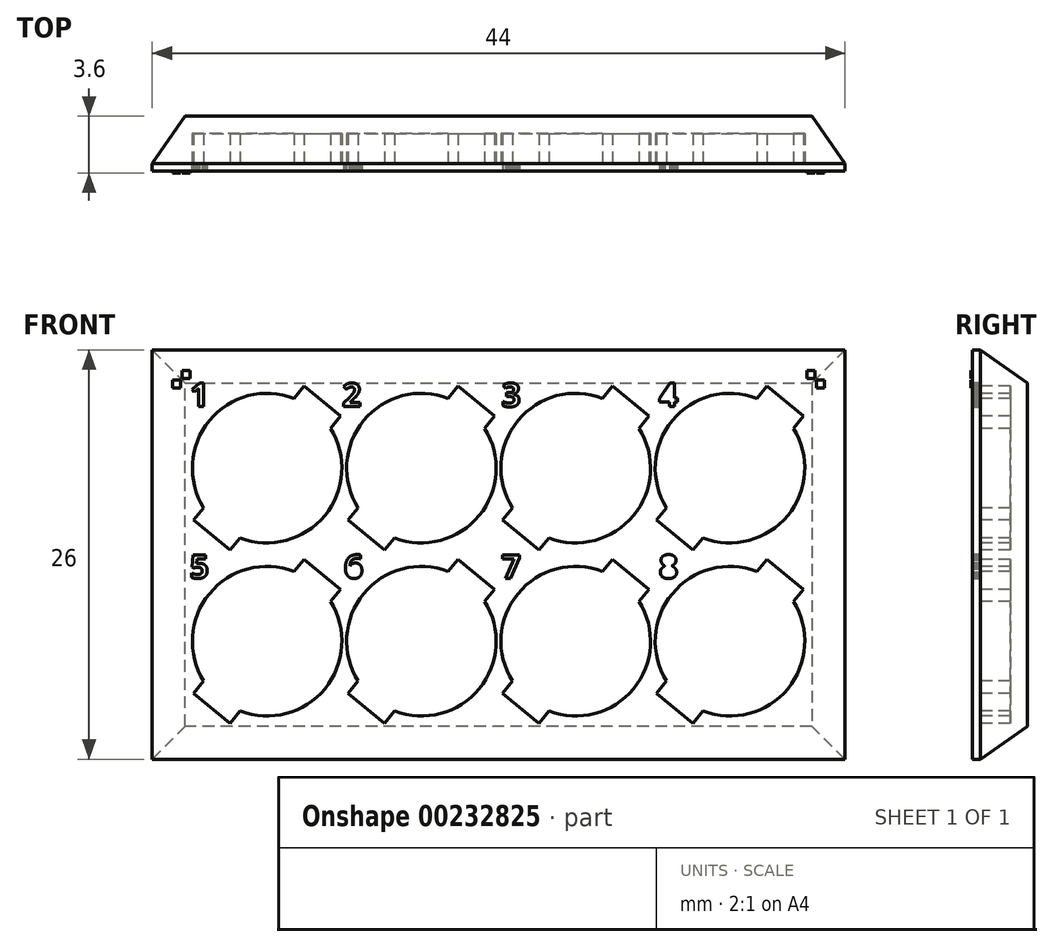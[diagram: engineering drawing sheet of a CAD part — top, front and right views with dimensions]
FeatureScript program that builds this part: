
annotation { "Feature Type Name" : "Feature", "Feature Type Description" : "" }
export const myFeature = defineFeature(function(context is Context, id is Id, definition is map)
    precondition{}
    {
        {
            var Q0;
            Q0=qCreatedBy(makeId("Front.planeOp"),FACE);
            var sketch = newSketch(context, id + "F0", { "sketchPlane" : qUnion([Q0])});
            skLineSegment(sketch, "E0.bottom", {"start": v(4.9, -5.5) * mm, "end": v(-4.9, -5.5) * mm});
            skLineSegment(sketch, "E0.top", {"start": v(4.9, 5.5) * mm, "end": v(-4.9, 5.5) * mm});
            skLineSegment(sketch, "E0.left", {"start": v(4.9, -5.5) * mm, "end": v(4.9, 5.5) * mm});
            skLineSegment(sketch, "E0.right", {"start": v(-4.9, -5.5) * mm, "end": v(-4.9, 5.5) * mm});
            skPoint(sketch, "E0.middle", {"position": v(0, 0) * mm});
            skSolve(sketch);
        }
        {
            var Q0;
            Q0=qSketchRegion(id+"F0",true);
            extrude(context, id + "F1", {"entities" : qUnion([Q0]), "oppositeDirection" : true, "depth" : 3.5 * mm, "offsetDistance" : 25 * mm});
        }
        {
            var Q0;
            Q0=qCreatedBy(makeId("Front.planeOp"),FACE);
            var sketch = newSketch(context, id + "F2", { "sketchPlane" : qUnion([Q0])});
            skCircle(sketch, "E1", {"center": v(0, 0) * mm, "radius": 4.75 * mm});
            skLineSegment(sketch, "E2", {"start": v(1.7, 4.43) * mm, "end": v(2.34, 5.2) * mm});
            skLineSegment(sketch, "E3", {"start": v(2.34, 5.2) * mm, "end": v(4.66, 3.3) * mm});
            skLineSegment(sketch, "E4", {"start": v(4.66, 3.3) * mm, "end": v(4.02, 2.53) * mm});
            skLineSegment(sketch, "E5", {"start": v(-4.02, -2.53) * mm, "end": v(-4.66, -3.3) * mm});
            skLineSegment(sketch, "E6", {"start": v(-4.66, -3.3) * mm, "end": v(-2.34, -5.2) * mm});
            skLineSegment(sketch, "E7", {"start": v(-2.34, -5.2) * mm, "end": v(-1.7, -4.43) * mm});
            skSolve(sketch);
        }
        {
            var Q0;
            Q0=qSketchRegion(id+"F2",true);
            extrude(context, id + "F3", {"entities" : qUnion([Q0]), "operationType" : NewBodyOperationType.REMOVE, "oppositeDirection" : true, "depth" : 2.4 * mm, "offsetDistance" : 25 * mm});
        }
        {
            var Q0;
            Q0=makeQuery(id+"F1.opExtrude","SWEPT_BODY",BODY,{"disambiguationData":[OSD([sQuery(id+"F0.wireOp",EDGE,"E0.bottom"),sQuery(id+"F0.wireOp",EDGE,"E0.top"),sQuery(id+"F0.wireOp",EDGE,"E0.left"),sQuery(id+"F0.wireOp",EDGE,"E0.right")])]});
            transform(context, id + "F4", {"entities" : qUnion([Q0]), "transformType" : TransformType.TRANSLATION_3D, "dx" : -9.8 * mm, "dy" : 0 * mm, "dz" : 0 * mm, "makeCopy" : true});
        }
        {
            var Q0;
            Q0=makeQuery(id+"F1.opExtrude","SWEPT_BODY",BODY,{"disambiguationData":[OSD([sQuery(id+"F0.wireOp",EDGE,"E0.bottom"),sQuery(id+"F0.wireOp",EDGE,"E0.top"),sQuery(id+"F0.wireOp",EDGE,"E0.left"),sQuery(id+"F0.wireOp",EDGE,"E0.right")])]});
            transform(context, id + "F5", {"entities" : qUnion([Q0]), "transformType" : TransformType.TRANSLATION_3D, "dx" : 0 * mm, "dy" : 0 * mm, "dz" : 11 * mm, "makeCopy" : true});
        }
        {
            var Q0;
            Q0=makeQuery(id+"F1.opExtrude","SWEPT_BODY",BODY,{"disambiguationData":[OSD([sQuery(id+"F0.wireOp",EDGE,"E0.bottom"),sQuery(id+"F0.wireOp",EDGE,"E0.top"),sQuery(id+"F0.wireOp",EDGE,"E0.left"),sQuery(id+"F0.wireOp",EDGE,"E0.right")])]});
            transform(context, id + "F6", {"entities" : qUnion([Q0]), "transformType" : TransformType.TRANSLATION_3D, "dx" : -9.8 * mm, "dy" : 0 * mm, "dz" : 11 * mm, "makeCopy" : true});
        }
        {
            var Q0;
            Q0=makeQuery(id+"F1.opExtrude","SWEPT_BODY",BODY,{"disambiguationData":[OSD([sQuery(id+"F0.wireOp",EDGE,"E0.bottom"),sQuery(id+"F0.wireOp",EDGE,"E0.top"),sQuery(id+"F0.wireOp",EDGE,"E0.left"),sQuery(id+"F0.wireOp",EDGE,"E0.right")])]});
            var Q1;
            Q1=makeQuery(id+"F4.opPattern","COPY",BODY,{"derivedFrom":makeQuery(id+"F1.opExtrude","SWEPT_BODY",BODY,{"disambiguationData":[OSD([sQuery(id+"F0.wireOp",EDGE,"E0.bottom"),sQuery(id+"F0.wireOp",EDGE,"E0.top"),sQuery(id+"F0.wireOp",EDGE,"E0.left"),sQuery(id+"F0.wireOp",EDGE,"E0.right")])]}),"instanceName":"1"});
            var Q2;
            Q2=makeQuery(id+"F5.opPattern","COPY",BODY,{"derivedFrom":makeQuery(id+"F1.opExtrude","SWEPT_BODY",BODY,{"disambiguationData":[OSD([sQuery(id+"F0.wireOp",EDGE,"E0.bottom"),sQuery(id+"F0.wireOp",EDGE,"E0.top"),sQuery(id+"F0.wireOp",EDGE,"E0.left"),sQuery(id+"F0.wireOp",EDGE,"E0.right")])]}),"instanceName":"1"});
            var Q3;
            Q3=makeQuery(id+"F6.opPattern","COPY",BODY,{"derivedFrom":makeQuery(id+"F1.opExtrude","SWEPT_BODY",BODY,{"disambiguationData":[OSD([sQuery(id+"F0.wireOp",EDGE,"E0.bottom"),sQuery(id+"F0.wireOp",EDGE,"E0.top"),sQuery(id+"F0.wireOp",EDGE,"E0.left"),sQuery(id+"F0.wireOp",EDGE,"E0.right")])]}),"instanceName":"1"});
            booleanBodies(context, id + "F7", {"operationType" : BooleanOperationType.UNION, "tools" : qUnion([Q0, Q1, Q2, Q3])});
        }
        {
            var Q0;
            Q0=makeQuery(id+"F1.opExtrude","SWEPT_BODY",BODY,{"disambiguationData":[OSD([sQuery(id+"F0.wireOp",EDGE,"E0.bottom"),sQuery(id+"F0.wireOp",EDGE,"E0.top"),sQuery(id+"F0.wireOp",EDGE,"E0.left"),sQuery(id+"F0.wireOp",EDGE,"E0.right")])]});
            transform(context, id + "F8", {"entities" : qUnion([Q0]), "transformType" : TransformType.TRANSLATION_3D, "dx" : 19.6 * mm, "dy" : 0 * mm, "dz" : 0 * mm, "makeCopy" : true});
        }
        {
            var Q0;
            Q0=makeQuery(id+"F1.opExtrude","SWEPT_BODY",BODY,{"disambiguationData":[OSD([sQuery(id+"F0.wireOp",EDGE,"E0.bottom"),sQuery(id+"F0.wireOp",EDGE,"E0.top"),sQuery(id+"F0.wireOp",EDGE,"E0.left"),sQuery(id+"F0.wireOp",EDGE,"E0.right")])]});
            var Q1;
            Q1=makeQuery(id+"F8.opPattern","COPY",BODY,{"derivedFrom":makeQuery(id+"F1.opExtrude","SWEPT_BODY",BODY,{"disambiguationData":[OSD([sQuery(id+"F0.wireOp",EDGE,"E0.bottom"),sQuery(id+"F0.wireOp",EDGE,"E0.top"),sQuery(id+"F0.wireOp",EDGE,"E0.left"),sQuery(id+"F0.wireOp",EDGE,"E0.right")])]}),"instanceName":"1"});
            booleanBodies(context, id + "F9", {"operationType" : BooleanOperationType.UNION, "tools" : qUnion([Q0, Q1])});
        }
        {
            var Q0;
            {var subQ0=makeQuery(id+"F1.opExtrude","CAP_FACE",FACE,{"disambiguationData":[OSD([sQuery(id+"F0.wireOp",EDGE,"E0.bottom"),sQuery(id+"F0.wireOp",EDGE,"E0.top"),sQuery(id+"F0.wireOp",EDGE,"E0.left"),sQuery(id+"F0.wireOp",EDGE,"E0.right")])],"isStart":true});Q0=makeQuery(id+"F7.opBoolean","MERGE",FACE,{"derivedFrom":[subQ0,makeQuery(id+"F4.opPattern","COPY",FACE,{"derivedFrom":subQ0,"instanceName":"1"}),makeQuery(id+"F5.opPattern","COPY",FACE,{"derivedFrom":subQ0,"instanceName":"1"}),makeQuery(id+"F6.opPattern","COPY",FACE,{"derivedFrom":subQ0,"instanceName":"1"})]});}
            var sketch = newSketch(context, id + "F10", { "sketchPlane" : qUnion([Q0])});
            skText(sketch, "E8", { "text": "1", "fontName": "OpenSans-Bold.ttf"});
            skPoint(sketch, "E8.secondSnap0", {"position": v(-4.7, 14.9) * mm});
            skText(sketch, "E9", { "text": "2", "fontName": "OpenSans-Bold.ttf"});
            skPoint(sketch, "E9.secondSnap0", {"position": v(-3.03, 14.9) * mm});
            skText(sketch, "E10", { "text": "3", "fontName": "OpenSans-Bold.ttf"});
            skPoint(sketch, "E10.secondSnap0", {"position": v(-13.47, 3.02) * mm});
            skText(sketch, "E11", { "text": "4", "fontName": "OpenSans-Bold.ttf"});
            skText(sketch, "E12", { "text": "5", "fontName": "OpenSans-Bold.ttf"});
            skText(sketch, "E13", { "text": "6", "fontName": "OpenSans-Bold.ttf"});
            skText(sketch, "E14", { "text": "7", "fontName": "OpenSans-Bold.ttf"});
            skText(sketch, "E15", { "text": "8", "fontName": "OpenSans-Bold.ttf"});
            const initialGuessF10  = {"E8": [-0.0147, 0.0149, 1, 0, 0.0015], "E9": [-0.00502, 0.0149, 1, 0, 0.0015], "E10": [0.0051, 0.0149, 1, 0, 0.0015], "E11": [0.0151, 0.0149, 1, 0, 0.0015], "E12": [-0.0147, 0.004, 1, 0, 0.0015], "E13": [-0.0049, 0.004, 1, 0, 0.0015], "E14": [0.0051, 0.004, 1, 0, 0.0015], "E15": [0.0151, 0.004, 1, 0, 0.0015]};
            skSetInitialGuess(sketch, initialGuessF10);
            skSolve(sketch);
        }
        {
            var Q0;
            Q0=qSketchRegion(id+"F10",true);
            extrude(context, id + "F11", {"entities" : qUnion([Q0]), "operationType" : NewBodyOperationType.REMOVE, "oppositeDirection" : true, "depth" : 0.5 * mm, "offsetDistance" : 25 * mm});
        }
        {
            var Q0;
            Q0=makeQuery(id+"F10.imprint","IMPRINT",FACE,{"disambiguationData":[TD([[makeQuery(id+"F10.imprint","IMPRINT",EDGE,{"derivedFrom":sQuery(id+"F10.wireOp",EDGE,"E11.sketch_text.stroke-11")}),1.0]])]});
            var Q1;
            Q1=makeQuery(id+"F10.imprint","IMPRINT",FACE,{"disambiguationData":[TD([[makeQuery(id+"F10.imprint","IMPRINT",EDGE,{"derivedFrom":sQuery(id+"F10.wireOp",EDGE,"E15.sketch_text.stroke-23")}),1.0]])]});
            var Q2;
            Q2=makeQuery(id+"F10.imprint","IMPRINT",FACE,{"disambiguationData":[TD([[makeQuery(id+"F10.imprint","IMPRINT",EDGE,{"derivedFrom":sQuery(id+"F10.wireOp",EDGE,"E15.sketch_text.stroke-16")}),1.0]])]});
            var Q3;
            Q3=makeQuery(id+"F10.imprint","IMPRINT",FACE,{"disambiguationData":[TD([[makeQuery(id+"F10.imprint","IMPRINT",EDGE,{"derivedFrom":sQuery(id+"F10.wireOp",EDGE,"E13.sketch_text.stroke-17")}),1.0]])]});
            var Q4;
            Q4=makeQuery(id+"F11.opExtrude","CAP_FACE",FACE,{"disambiguationData":[OSD([sQuery(id+"F10.wireOp",EDGE,"E11.sketch_text.stroke-0"),sQuery(id+"F10.wireOp",EDGE,"E11.sketch_text.stroke-1"),sQuery(id+"F10.wireOp",EDGE,"E11.sketch_text.stroke-2"),sQuery(id+"F10.wireOp",EDGE,"E11.sketch_text.stroke-3"),sQuery(id+"F10.wireOp",EDGE,"E11.sketch_text.stroke-4"),sQuery(id+"F10.wireOp",EDGE,"E11.sketch_text.stroke-5"),sQuery(id+"F10.wireOp",EDGE,"E11.sketch_text.stroke-6"),sQuery(id+"F10.wireOp",EDGE,"E11.sketch_text.stroke-7"),sQuery(id+"F10.wireOp",EDGE,"E11.sketch_text.stroke-8"),sQuery(id+"F10.wireOp",EDGE,"E11.sketch_text.stroke-9"),sQuery(id+"F10.wireOp",EDGE,"E11.sketch_text.stroke-10"),sQuery(id+"F10.wireOp",EDGE,"E11.sketch_text.stroke-11"),sQuery(id+"F10.wireOp",EDGE,"E11.sketch_text.stroke-12"),sQuery(id+"F10.wireOp",EDGE,"E11.sketch_text.stroke-13"),sQuery(id+"F10.wireOp",EDGE,"E11.sketch_text.stroke-14"),sQuery(id+"F10.wireOp",EDGE,"E11.sketch_text.stroke-15"),sQuery(id+"F10.wireOp",EDGE,"E11.sketch_text.stroke-16"),sQuery(id+"F10.wireOp",EDGE,"E11.sketch_text.stroke-17")])],"isStart":false});
            extrude(context, id + "F12", {"entities" : qUnion([Q0, Q1, Q2, Q3]), "operationType" : NewBodyOperationType.REMOVE, "oppositeDirection" : true, "endBoundEntityFace" : qUnion([Q4]), "depth" : 0.5 * mm, "offsetDistance" : 25 * mm});
        }
        {
            var Q0;
            {var subQ0=makeQuery(id+"F1.opExtrude","SWEPT_FACE",FACE,{"disambiguationData":[OSD([sQuery(id+"F0.wireOp",EDGE,"E0.right")])]});Q0=makeQuery(id+"F7.opBoolean","MERGE",FACE,{"derivedFrom":[makeQuery(id+"F4.opPattern","COPY",FACE,{"derivedFrom":subQ0,"instanceName":"1"}),makeQuery(id+"F6.opPattern","COPY",FACE,{"derivedFrom":subQ0,"instanceName":"1"})]});}
            extrude(context, id + "F13", {"entities" : qUnion([Q0]), "operationType" : NewBodyOperationType.ADD, "depth" : 2.4 * mm, "offsetDistance" : 25 * mm});
        }
        {
            var Q0;
            {var subQ0=sQuery(id+"F0.wireOp",EDGE,"E0.top");var subQ1=makeQuery(id+"F1.opExtrude","SWEPT_FACE",FACE,{"disambiguationData":[OSD([subQ0])]});var subQ2=makeQuery(id+"F7.opBoolean","MERGE",FACE,{"derivedFrom":[makeQuery(id+"F5.opPattern","COPY",FACE,{"derivedFrom":subQ1,"instanceName":"1"}),makeQuery(id+"F6.opPattern","COPY",FACE,{"derivedFrom":subQ1,"instanceName":"1"})]});Q0=makeQuery(id+"F13.boolean.opBoolean","MERGE",FACE,{"derivedFrom":[makeQuery(id+"F9.opBoolean","MERGE",FACE,{"derivedFrom":[subQ2,makeQuery(id+"F8.opPattern","COPY",FACE,{"derivedFrom":subQ2,"instanceName":"1"})]}),makeQuery(id+"F13.opExtrude","SWEPT_FACE",FACE,{"disambiguationData":[OSD([subQ0,sQuery(id+"F0.wireOp",EDGE,"E0.right")])]})]});}
            extrude(context, id + "F14", {"entities" : qUnion([Q0]), "operationType" : NewBodyOperationType.ADD, "depth" : 2 * mm, "offsetDistance" : 25 * mm});
        }
        {
            var Q0;
            {var subQ0=sQuery(id+"F0.wireOp",EDGE,"E0.bottom");var subQ1=makeQuery(id+"F1.opExtrude","SWEPT_FACE",FACE,{"disambiguationData":[OSD([subQ0])]});var subQ2=makeQuery(id+"F7.opBoolean","MERGE",FACE,{"derivedFrom":[subQ1,makeQuery(id+"F4.opPattern","COPY",FACE,{"derivedFrom":subQ1,"instanceName":"1"})]});Q0=makeQuery(id+"F13.boolean.opBoolean","MERGE",FACE,{"derivedFrom":[makeQuery(id+"F9.opBoolean","MERGE",FACE,{"derivedFrom":[subQ2,makeQuery(id+"F8.opPattern","COPY",FACE,{"derivedFrom":subQ2,"instanceName":"1"})]}),makeQuery(id+"F13.opExtrude","SWEPT_FACE",FACE,{"disambiguationData":[OSD([subQ0,sQuery(id+"F0.wireOp",EDGE,"E0.right")])]})]});}
            extrude(context, id + "F15", {"entities" : qUnion([Q0]), "operationType" : NewBodyOperationType.ADD, "depth" : 2 * mm, "offsetDistance" : 25 * mm});
        }
        {
            var Q0;
            {var subQ0=sQuery(id+"F0.wireOp",EDGE,"E0.left");var subQ1=makeQuery(id+"F1.opExtrude","SWEPT_FACE",FACE,{"disambiguationData":[OSD([subQ0])]});Q0=makeQuery(id+"F15.boolean.opBoolean","MERGE",FACE,{"derivedFrom":[makeQuery(id+"F14.boolean.opBoolean","MERGE",FACE,{"derivedFrom":[makeQuery(id+"F8.opPattern","COPY",FACE,{"derivedFrom":makeQuery(id+"F7.opBoolean","MERGE",FACE,{"derivedFrom":[subQ1,makeQuery(id+"F5.opPattern","COPY",FACE,{"derivedFrom":subQ1,"instanceName":"1"})]}),"instanceName":"1"}),makeQuery(id+"F14.opExtrude","SWEPT_FACE",FACE,{"disambiguationData":[OSD([sQuery(id+"F0.wireOp",EDGE,"E0.top"),subQ0])]})]}),makeQuery(id+"F15.opExtrude","SWEPT_FACE",FACE,{"disambiguationData":[OSD([sQuery(id+"F0.wireOp",EDGE,"E0.bottom"),subQ0])]})]});}
            var Q1;
            {var subQ0=sQuery(id+"F0.wireOp",EDGE,"E0.right");var subQ1=sQuery(id+"F0.wireOp",EDGE,"E0.bottom");var subQ2=makeQuery(id+"F1.opExtrude","CAP_EDGE",EDGE,{"disambiguationData":[OSD([subQ1])],"isStart":true});var subQ3=makeQuery(id+"F7.opBoolean","MERGE",EDGE,{"derivedFrom":[subQ2,makeQuery(id+"F4.opPattern","COPY",EDGE,{"derivedFrom":subQ2,"instanceName":"1"})]});var subQ4=sQuery(id+"F0.wireOp",EDGE,"E0.top");var subQ5=makeQuery(id+"F1.opExtrude","CAP_EDGE",EDGE,{"disambiguationData":[OSD([subQ4])],"isStart":true});var subQ6=makeQuery(id+"F7.opBoolean","MERGE",EDGE,{"derivedFrom":[makeQuery(id+"F5.opPattern","COPY",EDGE,{"derivedFrom":subQ5,"instanceName":"1"}),makeQuery(id+"F6.opPattern","COPY",EDGE,{"derivedFrom":subQ5,"instanceName":"1"})]});var subQ7=makeQuery(id+"F1.opExtrude","CAP_EDGE",EDGE,{"disambiguationData":[OSD([subQ0])],"isStart":true});var subQ22=makeQuery(id+"F1.opExtrude","SWEPT_FACE",FACE,{"disambiguationData":[OSD([subQ1])]});var subQ51=sQuery(id+"F0.wireOp",EDGE,"E0.left");var subQ53=makeQuery(id+"F1.opExtrude","CAP_FACE",FACE,{"disambiguationData":[OSD([subQ1,subQ4,subQ51,subQ0])],"isStart":true});var subQ54=makeQuery(id+"F7.opBoolean","MERGE",FACE,{"derivedFrom":[subQ53,makeQuery(id+"F4.opPattern","COPY",FACE,{"derivedFrom":subQ53,"instanceName":"1"}),makeQuery(id+"F5.opPattern","COPY",FACE,{"derivedFrom":subQ53,"instanceName":"1"}),makeQuery(id+"F6.opPattern","COPY",FACE,{"derivedFrom":subQ53,"instanceName":"1"})]});Q1=makeQuery(id+"F15.boolean.opBoolean","MERGE",FACE,{"derivedFrom":[makeQuery(id+"F14.boolean.opBoolean","MERGE",FACE,{"derivedFrom":[makeQuery(id+"F13.boolean.opBoolean","MERGE",FACE,{"derivedFrom":[makeQuery(id+"F11.boolean.opBoolean","SPLIT",FACE,{"disambiguationData":[TD([subQ22])],"derivedFrom":makeQuery(id+"F9.opBoolean","MERGE",FACE,{"derivedFrom":[subQ54,makeQuery(id+"F8.opPattern","COPY",FACE,{"derivedFrom":subQ54,"instanceName":"1"})]})}),makeQuery(id+"F13.opExtrude","SWEPT_FACE",FACE,{"disambiguationData":[OSD([subQ0]),TDD([makeQuery(id+"F7.opBoolean","MERGE",EDGE,{"derivedFrom":[makeQuery(id+"F4.opPattern","COPY",EDGE,{"derivedFrom":subQ7,"instanceName":"1"}),makeQuery(id+"F6.opPattern","COPY",EDGE,{"derivedFrom":subQ7,"instanceName":"1"})]})])]})]}),makeQuery(id+"F14.opExtrude","SWEPT_FACE",FACE,{"disambiguationData":[OSD([subQ4,subQ0]),TDD([makeQuery(id+"F13.boolean.opBoolean","MERGE",EDGE,{"derivedFrom":[makeQuery(id+"F9.opBoolean","MERGE",EDGE,{"derivedFrom":[subQ6,makeQuery(id+"F8.opPattern","COPY",EDGE,{"derivedFrom":subQ6,"instanceName":"1"})]}),makeQuery(id+"F13.opExtrude","SWEPT_EDGE",EDGE,{"disambiguationData":[OSD([subQ4,subQ0]),TDD([makeQuery(id+"F6.opPattern","COPY",VERTEX,{"derivedFrom":makeQuery(id+"F1.opExtrude","CAP_VERTEX",VERTEX,{"disambiguationData":[OSD([subQ4,subQ0])],"isStart":true}),"instanceName":"1"})])]})]})])]})]}),makeQuery(id+"F15.opExtrude","SWEPT_FACE",FACE,{"disambiguationData":[OSD([subQ1,subQ0]),TDD([makeQuery(id+"F13.boolean.opBoolean","MERGE",EDGE,{"derivedFrom":[makeQuery(id+"F9.opBoolean","MERGE",EDGE,{"derivedFrom":[subQ3,makeQuery(id+"F8.opPattern","COPY",EDGE,{"derivedFrom":subQ3,"instanceName":"1"})]}),makeQuery(id+"F13.opExtrude","SWEPT_EDGE",EDGE,{"disambiguationData":[OSD([subQ1,subQ0]),TDD([makeQuery(id+"F4.opPattern","COPY",VERTEX,{"derivedFrom":makeQuery(id+"F1.opExtrude","CAP_VERTEX",VERTEX,{"disambiguationData":[OSD([subQ1,subQ0])],"isStart":true}),"instanceName":"1"})])]})]})])]})]});}
            extrude(context, id + "F16", {"entities" : qUnion([Q0]), "operationType" : NewBodyOperationType.ADD, "depth" : 2.4 * mm, "offsetDistance" : 25 * mm});
        }
        {
            var Q0;
            {var subQ0=sQuery(id+"F0.wireOp",EDGE,"E0.left");var subQ1=sQuery(id+"F0.wireOp",EDGE,"E0.bottom");var subQ2=sQuery(id+"F0.wireOp",EDGE,"E0.top");var subQ3=makeQuery(id+"F1.opExtrude","CAP_EDGE",EDGE,{"disambiguationData":[OSD([subQ0])],"isStart":true});var subQ4=sQuery(id+"F0.wireOp",EDGE,"E0.right");var subQ5=makeQuery(id+"F1.opExtrude","CAP_EDGE",EDGE,{"disambiguationData":[OSD([subQ1])],"isStart":true});var subQ6=makeQuery(id+"F7.opBoolean","MERGE",EDGE,{"derivedFrom":[subQ5,makeQuery(id+"F4.opPattern","COPY",EDGE,{"derivedFrom":subQ5,"instanceName":"1"})]});var subQ7=makeQuery(id+"F1.opExtrude","CAP_EDGE",EDGE,{"disambiguationData":[OSD([subQ2])],"isStart":true});var subQ8=makeQuery(id+"F7.opBoolean","MERGE",EDGE,{"derivedFrom":[makeQuery(id+"F5.opPattern","COPY",EDGE,{"derivedFrom":subQ7,"instanceName":"1"}),makeQuery(id+"F6.opPattern","COPY",EDGE,{"derivedFrom":subQ7,"instanceName":"1"})]});var subQ9=makeQuery(id+"F1.opExtrude","CAP_EDGE",EDGE,{"disambiguationData":[OSD([subQ4])],"isStart":true});var subQ24=makeQuery(id+"F1.opExtrude","SWEPT_FACE",FACE,{"disambiguationData":[OSD([subQ1])]});var subQ54=makeQuery(id+"F1.opExtrude","CAP_FACE",FACE,{"disambiguationData":[OSD([subQ1,subQ2,subQ0,subQ4])],"isStart":true});var subQ55=makeQuery(id+"F7.opBoolean","MERGE",FACE,{"derivedFrom":[subQ54,makeQuery(id+"F4.opPattern","COPY",FACE,{"derivedFrom":subQ54,"instanceName":"1"}),makeQuery(id+"F5.opPattern","COPY",FACE,{"derivedFrom":subQ54,"instanceName":"1"}),makeQuery(id+"F6.opPattern","COPY",FACE,{"derivedFrom":subQ54,"instanceName":"1"})]});Q0=makeQuery(id+"F16.boolean.opBoolean","MERGE",FACE,{"derivedFrom":[makeQuery(id+"F15.boolean.opBoolean","MERGE",FACE,{"derivedFrom":[makeQuery(id+"F14.boolean.opBoolean","MERGE",FACE,{"derivedFrom":[makeQuery(id+"F13.boolean.opBoolean","MERGE",FACE,{"derivedFrom":[makeQuery(id+"F11.boolean.opBoolean","SPLIT",FACE,{"disambiguationData":[TD([subQ24])],"derivedFrom":makeQuery(id+"F9.opBoolean","MERGE",FACE,{"derivedFrom":[subQ55,makeQuery(id+"F8.opPattern","COPY",FACE,{"derivedFrom":subQ55,"instanceName":"1"})]})}),makeQuery(id+"F13.opExtrude","SWEPT_FACE",FACE,{"disambiguationData":[OSD([subQ4]),TDD([makeQuery(id+"F7.opBoolean","MERGE",EDGE,{"derivedFrom":[makeQuery(id+"F4.opPattern","COPY",EDGE,{"derivedFrom":subQ9,"instanceName":"1"}),makeQuery(id+"F6.opPattern","COPY",EDGE,{"derivedFrom":subQ9,"instanceName":"1"})]})])]})]}),makeQuery(id+"F14.opExtrude","SWEPT_FACE",FACE,{"disambiguationData":[OSD([subQ2,subQ4]),TDD([makeQuery(id+"F13.boolean.opBoolean","MERGE",EDGE,{"derivedFrom":[makeQuery(id+"F9.opBoolean","MERGE",EDGE,{"derivedFrom":[subQ8,makeQuery(id+"F8.opPattern","COPY",EDGE,{"derivedFrom":subQ8,"instanceName":"1"})]}),makeQuery(id+"F13.opExtrude","SWEPT_EDGE",EDGE,{"disambiguationData":[OSD([subQ2,subQ4]),TDD([makeQuery(id+"F6.opPattern","COPY",VERTEX,{"derivedFrom":makeQuery(id+"F1.opExtrude","CAP_VERTEX",VERTEX,{"disambiguationData":[OSD([subQ2,subQ4])],"isStart":true}),"instanceName":"1"})])]})]})])]})]}),makeQuery(id+"F15.opExtrude","SWEPT_FACE",FACE,{"disambiguationData":[OSD([subQ1,subQ4]),TDD([makeQuery(id+"F13.boolean.opBoolean","MERGE",EDGE,{"derivedFrom":[makeQuery(id+"F9.opBoolean","MERGE",EDGE,{"derivedFrom":[subQ6,makeQuery(id+"F8.opPattern","COPY",EDGE,{"derivedFrom":subQ6,"instanceName":"1"})]}),makeQuery(id+"F13.opExtrude","SWEPT_EDGE",EDGE,{"disambiguationData":[OSD([subQ1,subQ4]),TDD([makeQuery(id+"F4.opPattern","COPY",VERTEX,{"derivedFrom":makeQuery(id+"F1.opExtrude","CAP_VERTEX",VERTEX,{"disambiguationData":[OSD([subQ1,subQ4])],"isStart":true}),"instanceName":"1"})])]})]})])]})]}),makeQuery(id+"F16.opExtrude","SWEPT_FACE",FACE,{"disambiguationData":[OSD([subQ1,subQ2,subQ0]),TDD([makeQuery(id+"F15.boolean.opBoolean","MERGE",EDGE,{"derivedFrom":[makeQuery(id+"F14.boolean.opBoolean","MERGE",EDGE,{"derivedFrom":[makeQuery(id+"F8.opPattern","COPY",EDGE,{"derivedFrom":makeQuery(id+"F7.opBoolean","MERGE",EDGE,{"derivedFrom":[subQ3,makeQuery(id+"F5.opPattern","COPY",EDGE,{"derivedFrom":subQ3,"instanceName":"1"})]}),"instanceName":"1"}),makeQuery(id+"F14.opExtrude","SWEPT_EDGE",EDGE,{"disambiguationData":[OSD([subQ2,subQ0]),TDD([makeQuery(id+"F8.opPattern","COPY",VERTEX,{"derivedFrom":makeQuery(id+"F5.opPattern","COPY",VERTEX,{"derivedFrom":makeQuery(id+"F1.opExtrude","CAP_VERTEX",VERTEX,{"disambiguationData":[OSD([subQ2,subQ0])],"isStart":true}),"instanceName":"1"}),"instanceName":"1"})])]})]}),makeQuery(id+"F15.opExtrude","SWEPT_EDGE",EDGE,{"disambiguationData":[OSD([subQ1,subQ0]),TDD([makeQuery(id+"F8.opPattern","COPY",VERTEX,{"derivedFrom":makeQuery(id+"F1.opExtrude","CAP_VERTEX",VERTEX,{"disambiguationData":[OSD([subQ1,subQ0])],"isStart":true}),"instanceName":"1"})])]})]})])]})]});}
            var sketch = newSketch(context, id + "F17", { "sketchPlane" : qUnion([Q0])});
            skLineSegment(sketch, "E16.bottom", {"start": v(-15.2, 17.2) * mm, "end": v(-14.7, 17.2) * mm});
            skLineSegment(sketch, "E16.top", {"start": v(-15.2, 16.7) * mm, "end": v(-14.7, 16.7) * mm});
            skLineSegment(sketch, "E16.left", {"start": v(-15.2, 17.2) * mm, "end": v(-15.2, 16.7) * mm});
            skLineSegment(sketch, "E16.right", {"start": v(-14.7, 17.2) * mm, "end": v(-14.7, 16.7) * mm});
            skLineSegment(sketch, "E17.bottom", {"start": v(-15.8, 16.6) * mm, "end": v(-15.3, 16.6) * mm});
            skLineSegment(sketch, "E17.top", {"start": v(-15.8, 16.1) * mm, "end": v(-15.3, 16.1) * mm});
            skLineSegment(sketch, "E17.left", {"start": v(-15.8, 16.6) * mm, "end": v(-15.8, 16.1) * mm});
            skLineSegment(sketch, "E17.right", {"start": v(-15.3, 16.6) * mm, "end": v(-15.3, 16.1) * mm});
            skPoint(sketch, "E18.oppositeSnap0", {"position": v(23.94, 13.91) * mm});
            skLineSegment(sketch, "E18.bottom", {"start": v(24.5, 17.2) * mm, "end": v(25, 17.2) * mm});
            skLineSegment(sketch, "E18.top", {"start": v(24.5, 16.7) * mm, "end": v(25, 16.7) * mm});
            skLineSegment(sketch, "E18.left", {"start": v(24.5, 17.2) * mm, "end": v(24.5, 16.7) * mm});
            skLineSegment(sketch, "E18.right", {"start": v(25, 17.2) * mm, "end": v(25, 16.7) * mm});
            skLineSegment(sketch, "E19.bottom", {"start": v(25.1, 16.6) * mm, "end": v(25.6, 16.6) * mm});
            skLineSegment(sketch, "E19.top", {"start": v(25.1, 16.1) * mm, "end": v(25.6, 16.1) * mm});
            skLineSegment(sketch, "E19.left", {"start": v(25.1, 16.6) * mm, "end": v(25.1, 16.1) * mm});
            skLineSegment(sketch, "E19.right", {"start": v(25.6, 16.6) * mm, "end": v(25.6, 16.1) * mm});
            skLineSegment(sketch, "E20.bottom", {"start": v(25.1, -5.1) * mm, "end": v(25.6, -5.1) * mm});
            skLineSegment(sketch, "E20.top", {"start": v(25.1, -5.6) * mm, "end": v(25.6, -5.6) * mm});
            skLineSegment(sketch, "E20.left", {"start": v(25.1, -5.1) * mm, "end": v(25.1, -5.6) * mm});
            skLineSegment(sketch, "E20.right", {"start": v(25.6, -5.1) * mm, "end": v(25.6, -5.6) * mm});
            skLineSegment(sketch, "E21.bottom", {"start": v(-15.8, -5.1) * mm, "end": v(-15.3, -5.1) * mm});
            skLineSegment(sketch, "E21.top", {"start": v(-15.8, -5.6) * mm, "end": v(-15.3, -5.6) * mm});
            skLineSegment(sketch, "E21.left", {"start": v(-15.8, -5.1) * mm, "end": v(-15.8, -5.6) * mm});
            skLineSegment(sketch, "E21.right", {"start": v(-15.3, -5.1) * mm, "end": v(-15.3, -5.6) * mm});
            skLineSegment(sketch, "E22.bottom", {"start": v(-15.2, -5.7) * mm, "end": v(-14.7, -5.7) * mm});
            skLineSegment(sketch, "E22.top", {"start": v(-15.2, -6.2) * mm, "end": v(-14.7, -6.2) * mm});
            skLineSegment(sketch, "E22.left", {"start": v(-15.2, -5.7) * mm, "end": v(-15.2, -6.2) * mm});
            skLineSegment(sketch, "E22.right", {"start": v(-14.7, -5.7) * mm, "end": v(-14.7, -6.2) * mm});
            skLineSegment(sketch, "E23.bottom", {"start": v(24.5, -5.7) * mm, "end": v(25, -5.7) * mm});
            skLineSegment(sketch, "E23.top", {"start": v(24.5, -6.2) * mm, "end": v(25, -6.2) * mm});
            skLineSegment(sketch, "E23.left", {"start": v(24.5, -5.7) * mm, "end": v(24.5, -6.2) * mm});
            skLineSegment(sketch, "E23.right", {"start": v(25, -5.7) * mm, "end": v(25, -6.2) * mm});
            skSolve(sketch);
        }
        {
            var Q0;
            Q0=makeQuery(id+"F17.imprint","IMPRINT",FACE,{"disambiguationData":[TD([[makeQuery(id+"F17.imprint","IMPRINT",EDGE,{"derivedFrom":sQuery(id+"F17.wireOp",EDGE,"E18.bottom")}),-1.0]])]});
            var Q1;
            Q1=makeQuery(id+"F17.imprint","IMPRINT",FACE,{"disambiguationData":[TD([[makeQuery(id+"F17.imprint","IMPRINT",EDGE,{"derivedFrom":sQuery(id+"F17.wireOp",EDGE,"E19.bottom")}),-1.0]])]});
            var Q2;
            Q2=makeQuery(id+"F17.imprint","IMPRINT",FACE,{"disambiguationData":[TD([[makeQuery(id+"F17.imprint","IMPRINT",EDGE,{"derivedFrom":sQuery(id+"F17.wireOp",EDGE,"E16.bottom")}),-1.0]])]});
            var Q3;
            Q3=makeQuery(id+"F17.imprint","IMPRINT",FACE,{"disambiguationData":[TD([[makeQuery(id+"F17.imprint","IMPRINT",EDGE,{"derivedFrom":sQuery(id+"F17.wireOp",EDGE,"E17.bottom")}),-1.0]])]});
            extrude(context, id + "F18", {"entities" : qUnion([Q0, Q1, Q2, Q3]), "operationType" : NewBodyOperationType.ADD, "endBound" : BoundingType.SYMMETRIC, "depth" : 0.2 * mm, "offsetDistance" : 25 * mm});
        }
        {
            var Q0;
            {var subQ0=sQuery(id+"F0.wireOp",EDGE,"E0.left");var subQ1=sQuery(id+"F0.wireOp",EDGE,"E0.bottom");var subQ2=sQuery(id+"F0.wireOp",EDGE,"E0.right");var subQ3=makeQuery(id+"F1.opExtrude","CAP_EDGE",EDGE,{"disambiguationData":[OSD([subQ1])],"isStart":false});var subQ4=makeQuery(id+"F7.opBoolean","MERGE",EDGE,{"derivedFrom":[subQ3,makeQuery(id+"F4.opPattern","COPY",EDGE,{"derivedFrom":subQ3,"instanceName":"1"})]});Q0=makeQuery(id+"F16.boolean.opBoolean","MERGE",EDGE,{"derivedFrom":[makeQuery(id+"F15.opExtrude","CAP_EDGE",EDGE,{"disambiguationData":[OSD([subQ1,subQ2]),TDD([makeQuery(id+"F13.boolean.opBoolean","MERGE",EDGE,{"derivedFrom":[makeQuery(id+"F9.opBoolean","MERGE",EDGE,{"derivedFrom":[subQ4,makeQuery(id+"F8.opPattern","COPY",EDGE,{"derivedFrom":subQ4,"instanceName":"1"})]}),makeQuery(id+"F13.opExtrude","SWEPT_EDGE",EDGE,{"disambiguationData":[OSD([subQ1,subQ2]),TDD([makeQuery(id+"F4.opPattern","COPY",VERTEX,{"derivedFrom":makeQuery(id+"F1.opExtrude","CAP_VERTEX",VERTEX,{"disambiguationData":[OSD([subQ1,subQ2])],"isStart":false}),"instanceName":"1"})])]})]})])],"isStart":false}),makeQuery(id+"F16.opExtrude","SWEPT_EDGE",EDGE,{"disambiguationData":[OSD([subQ1,subQ0]),TDD([makeQuery(id+"F15.opExtrude","CAP_VERTEX",VERTEX,{"disambiguationData":[OSD([subQ1,subQ0]),TDD([makeQuery(id+"F8.opPattern","COPY",VERTEX,{"derivedFrom":makeQuery(id+"F1.opExtrude","CAP_VERTEX",VERTEX,{"disambiguationData":[OSD([subQ1,subQ0])],"isStart":false}),"instanceName":"1"})])],"isStart":false})])]})]});}
            var Q1;
            {var subQ0=sQuery(id+"F0.wireOp",EDGE,"E0.left");var subQ1=sQuery(id+"F0.wireOp",EDGE,"E0.bottom");var subQ2=sQuery(id+"F0.wireOp",EDGE,"E0.top");var subQ3=makeQuery(id+"F1.opExtrude","CAP_EDGE",EDGE,{"disambiguationData":[OSD([subQ0])],"isStart":false});Q1=makeQuery(id+"F16.opExtrude","CAP_EDGE",EDGE,{"disambiguationData":[OSD([subQ1,subQ2,subQ0]),TDD([makeQuery(id+"F15.boolean.opBoolean","MERGE",EDGE,{"derivedFrom":[makeQuery(id+"F14.boolean.opBoolean","MERGE",EDGE,{"derivedFrom":[makeQuery(id+"F8.opPattern","COPY",EDGE,{"derivedFrom":makeQuery(id+"F7.opBoolean","MERGE",EDGE,{"derivedFrom":[subQ3,makeQuery(id+"F5.opPattern","COPY",EDGE,{"derivedFrom":subQ3,"instanceName":"1"})]}),"instanceName":"1"}),makeQuery(id+"F14.opExtrude","SWEPT_EDGE",EDGE,{"disambiguationData":[OSD([subQ2,subQ0]),TDD([makeQuery(id+"F8.opPattern","COPY",VERTEX,{"derivedFrom":makeQuery(id+"F5.opPattern","COPY",VERTEX,{"derivedFrom":makeQuery(id+"F1.opExtrude","CAP_VERTEX",VERTEX,{"disambiguationData":[OSD([subQ2,subQ0])],"isStart":false}),"instanceName":"1"}),"instanceName":"1"})])]})]}),makeQuery(id+"F15.opExtrude","SWEPT_EDGE",EDGE,{"disambiguationData":[OSD([subQ1,subQ0]),TDD([makeQuery(id+"F8.opPattern","COPY",VERTEX,{"derivedFrom":makeQuery(id+"F1.opExtrude","CAP_VERTEX",VERTEX,{"disambiguationData":[OSD([subQ1,subQ0])],"isStart":false}),"instanceName":"1"})])]})]})])],"isStart":false});}
            var Q2;
            {var subQ0=sQuery(id+"F0.wireOp",EDGE,"E0.left");var subQ1=sQuery(id+"F0.wireOp",EDGE,"E0.top");var subQ2=sQuery(id+"F0.wireOp",EDGE,"E0.right");var subQ3=makeQuery(id+"F1.opExtrude","CAP_EDGE",EDGE,{"disambiguationData":[OSD([subQ1])],"isStart":false});var subQ4=makeQuery(id+"F7.opBoolean","MERGE",EDGE,{"derivedFrom":[makeQuery(id+"F5.opPattern","COPY",EDGE,{"derivedFrom":subQ3,"instanceName":"1"}),makeQuery(id+"F6.opPattern","COPY",EDGE,{"derivedFrom":subQ3,"instanceName":"1"})]});Q2=makeQuery(id+"F16.boolean.opBoolean","MERGE",EDGE,{"derivedFrom":[makeQuery(id+"F14.opExtrude","CAP_EDGE",EDGE,{"disambiguationData":[OSD([subQ1,subQ2]),TDD([makeQuery(id+"F13.boolean.opBoolean","MERGE",EDGE,{"derivedFrom":[makeQuery(id+"F9.opBoolean","MERGE",EDGE,{"derivedFrom":[subQ4,makeQuery(id+"F8.opPattern","COPY",EDGE,{"derivedFrom":subQ4,"instanceName":"1"})]}),makeQuery(id+"F13.opExtrude","SWEPT_EDGE",EDGE,{"disambiguationData":[OSD([subQ1,subQ2]),TDD([makeQuery(id+"F6.opPattern","COPY",VERTEX,{"derivedFrom":makeQuery(id+"F1.opExtrude","CAP_VERTEX",VERTEX,{"disambiguationData":[OSD([subQ1,subQ2])],"isStart":false}),"instanceName":"1"})])]})]})])],"isStart":false}),makeQuery(id+"F16.opExtrude","SWEPT_EDGE",EDGE,{"disambiguationData":[OSD([subQ1,subQ0]),TDD([makeQuery(id+"F14.opExtrude","CAP_VERTEX",VERTEX,{"disambiguationData":[OSD([subQ1,subQ0]),TDD([makeQuery(id+"F8.opPattern","COPY",VERTEX,{"derivedFrom":makeQuery(id+"F5.opPattern","COPY",VERTEX,{"derivedFrom":makeQuery(id+"F1.opExtrude","CAP_VERTEX",VERTEX,{"disambiguationData":[OSD([subQ1,subQ0])],"isStart":false}),"instanceName":"1"}),"instanceName":"1"})])],"isStart":false})])]})]});}
            var Q3;
            {var subQ0=sQuery(id+"F0.wireOp",EDGE,"E0.right");var subQ1=sQuery(id+"F0.wireOp",EDGE,"E0.bottom");var subQ2=sQuery(id+"F0.wireOp",EDGE,"E0.top");var subQ3=makeQuery(id+"F1.opExtrude","CAP_EDGE",EDGE,{"disambiguationData":[OSD([subQ0])],"isStart":false});Q3=makeQuery(id+"F15.boolean.opBoolean","MERGE",EDGE,{"derivedFrom":[makeQuery(id+"F14.boolean.opBoolean","MERGE",EDGE,{"derivedFrom":[makeQuery(id+"F13.opExtrude","CAP_EDGE",EDGE,{"disambiguationData":[OSD([subQ0]),TDD([makeQuery(id+"F7.opBoolean","MERGE",EDGE,{"derivedFrom":[makeQuery(id+"F4.opPattern","COPY",EDGE,{"derivedFrom":subQ3,"instanceName":"1"}),makeQuery(id+"F6.opPattern","COPY",EDGE,{"derivedFrom":subQ3,"instanceName":"1"})]})])],"isStart":false}),makeQuery(id+"F14.opExtrude","SWEPT_EDGE",EDGE,{"disambiguationData":[OSD([subQ2,subQ0]),TDD([makeQuery(id+"F13.opExtrude","CAP_VERTEX",VERTEX,{"disambiguationData":[OSD([subQ2,subQ0]),TDD([makeQuery(id+"F6.opPattern","COPY",VERTEX,{"derivedFrom":makeQuery(id+"F1.opExtrude","CAP_VERTEX",VERTEX,{"disambiguationData":[OSD([subQ2,subQ0])],"isStart":false}),"instanceName":"1"})])],"isStart":false})])]})]}),makeQuery(id+"F15.opExtrude","SWEPT_EDGE",EDGE,{"disambiguationData":[OSD([subQ1,subQ0]),TDD([makeQuery(id+"F13.opExtrude","CAP_VERTEX",VERTEX,{"disambiguationData":[OSD([subQ1,subQ0]),TDD([makeQuery(id+"F4.opPattern","COPY",VERTEX,{"derivedFrom":makeQuery(id+"F1.opExtrude","CAP_VERTEX",VERTEX,{"disambiguationData":[OSD([subQ1,subQ0])],"isStart":false}),"instanceName":"1"})])],"isStart":false})])]})]});}
            chamfer(context, id + "F19", {"entities" : qUnion([Q0, Q1, Q2, Q3]), "chamferType" : ChamferType.OFFSET_ANGLE, "width" : 2.1 * mm, "oppositeDirection" : false, "angle" : 55 * degree, "tangentPropagation" : true});
        }
    });
